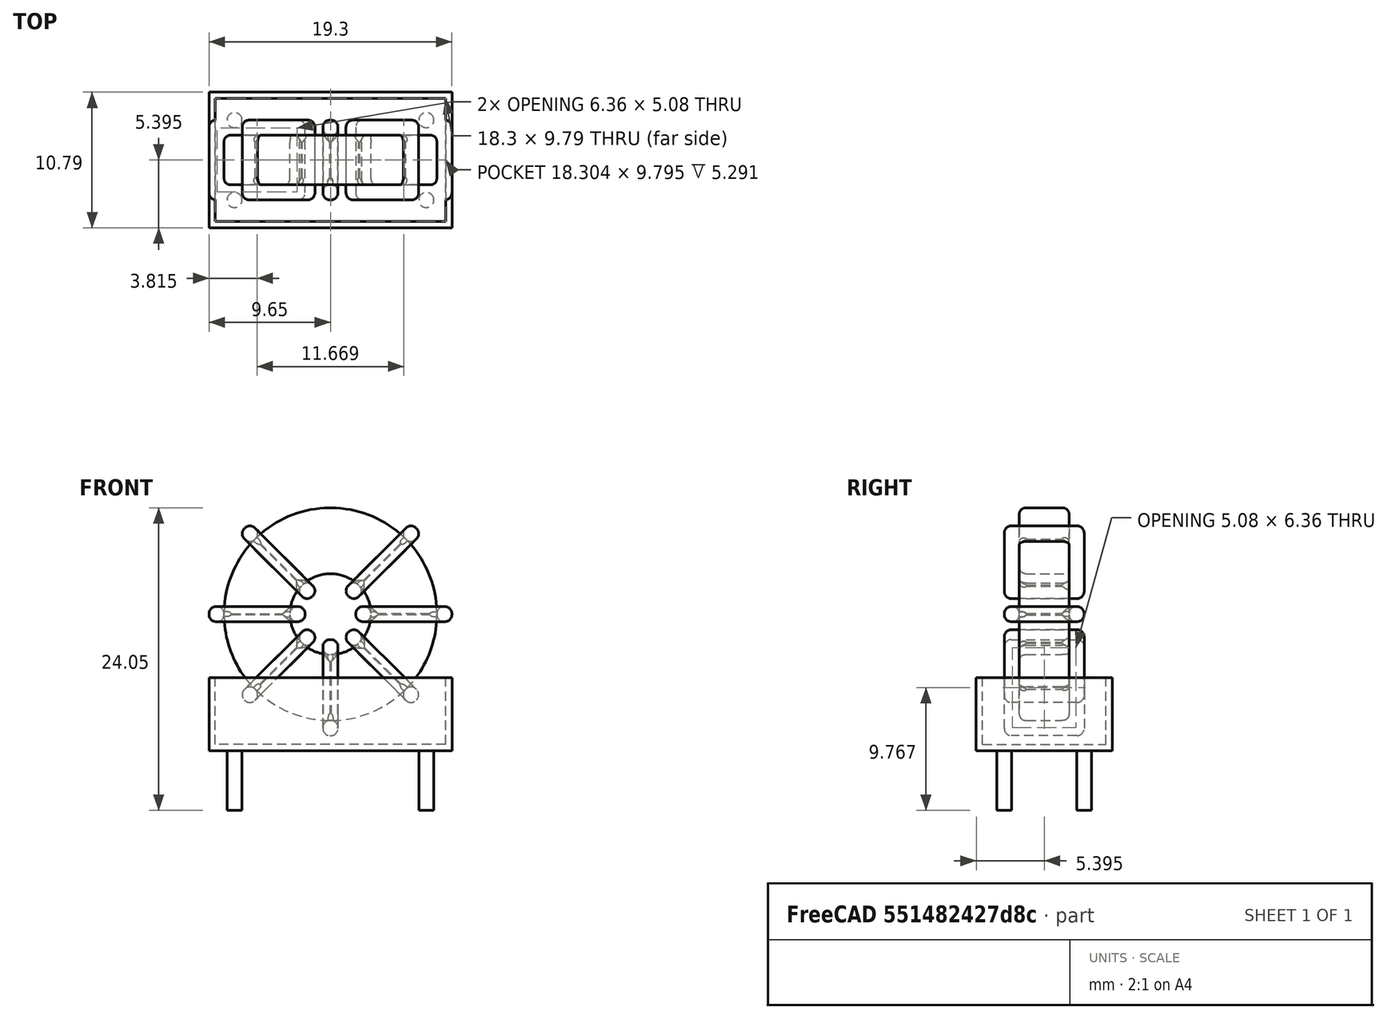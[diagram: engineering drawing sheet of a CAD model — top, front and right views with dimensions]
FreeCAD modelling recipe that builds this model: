
FCSTD DOCUMENT  (FreeCAD 0.16R6712 (Git))
Label: L_CommonMode_Toroid_Vertical_L19.3mm_W10.8mm_Px6.35mm_Py15.24mm_Bourns_8100
License: All rights reserved
LicenseURL: http://en.wikipedia.org/wiki/All_rights_reserved
objects: Sketcher::SketchObject×8, PartDesign::Pad×8, PartDesign::Fillet×5, Spreadsheet::Sheet×1, Part::MultiFuse×1
note: 30 computed .brp shape members not serialized (recipe doc carries the construction recipe); baked Part::Feature solids carry a one-line shape summary decoded from their .brp

FEATURE [Spreadsheet::Sheet] Spreadsheet  label="dimensions"
  cells = A1=Wx; B1(Wx)=19.304; C1(WW)=6.434666666666666; D1(iWx)=19.304; A2=Wy; B2(Wy)=6.35; D2(iWy)=10.795; A3=RM; B3(RMx)=6.35; C3(RMy)=15.24; A4=d_wire; B4(d_wire)=1.2; A5=H; B5(H)=31; A6=offsetx; B6(offsetx)=2.032
FEATURE [Sketcher::SketchObject] Sketch
  Placement = pos=(7.62,-3.175,0) rot=(1,0,0;1.5708rad)
  expr: Placement.Base.x = Spreadsheet.RMy / 2
  expr: Constraints[4] = Spreadsheet.WW / 2
  expr: Placement.Base.y = -Spreadsheet.RMx / 2
  expr: Constraints[0] = Spreadsheet.Wx / 2 - Spreadsheet.d_wire
  expr: Constraints[2] = Spreadsheet.Wx / 2 + Spreadsheet.d_wire + 0.5
  sketch-geometry (2):
    g0: Circle CenterX=0 CenterY=11.352 CenterZ=0 NormalX=0 NormalY=0 NormalZ=1 Radius=8.452
    g1: Circle CenterX=0 CenterY=11.352 CenterZ=0 NormalX=0 NormalY=0 NormalZ=1 Radius=3.21733
  constraints (5):
    c: Radius(g0) = 8.452
    c: DistanceX(g-1,g0) = 0
    c: DistanceY(g-1,g0) = 11.352
    c: Coincident(g1,g0)
    c: Radius(g1) = 3.21733
FEATURE [PartDesign::Pad] Pad
  Length = 3.95
  Length2 = 100
  Midplane = true
  Placement = pos=(7.62,-3.175,0) rot=(1,0,0;1.5708rad)
  Sketch = -> Sketch
  Type = 0
  expr: Length = Spreadsheet.Wy - 2 * Spreadsheet.d_wire
FEATURE [Sketcher::SketchObject] Sketch001
  Placement = pos=(0,0,0.75) rot=(0,0,1;0rad)
  expr: Constraints[4] = Spreadsheet.RMy
  expr: Constraints[2] = -Spreadsheet.RMx
  expr: Constraints[1] = Spreadsheet.d_wire / 2
  sketch-geometry (4):
    g0: Circle CenterX=0 CenterY=0 CenterZ=0 NormalX=0 NormalY=0 NormalZ=1 Radius=0.6
    g1: Circle CenterX=15.24 CenterY=-6.35 CenterZ=0 NormalX=0 NormalY=0 NormalZ=1 Radius=0.6
    g2: Circle CenterX=0 CenterY=-6.35 CenterZ=0 NormalX=0 NormalY=0 NormalZ=1 Radius=0.6
    g3: Circle CenterX=15.24 CenterY=0 CenterZ=0 NormalX=0 NormalY=0 NormalZ=1 Radius=0.6
  constraints (11):
    c: Equal(g0,g1)
    c: Radius(g0) = 0.6
    c: DistanceY(g-1,g1) = -6.35
    c: Coincident(g0,g-1)
    c: DistanceX(g-1,g1) = 15.24
    c: PointOnObject(g2,g-2)
    c: DistanceY(g-1,g3) = 0
    c: DistanceY(g2,g1) = 0
    c: DistanceX(g3,g1) = 0
    c: Equal(g3,g2)
    c: Equal(g2,g1)
FEATURE [PartDesign::Pad] Pad001
  Length = 5
  Length2 = 0
  Placement = pos=(0,0,0.75) rot=(0,0,1;0rad)
  Reversed = true
  Sketch = -> Sketch001
  Type = 0
FEATURE [PartDesign::Fillet] Fillet
  Base = -> Pad [Edge6,Edge3,Edge2]
  Placement = pos=(7.62,-3.175,0) rot=(1,0,0;1.5708rad)
  Radius = 0.5
FEATURE [Sketcher::SketchObject] Sketch003
  Placement = pos=(7.62,0,11.352) rot=(1,0,0;3.14159rad)
  expr: Placement.Base.x = Spreadsheet.RMy / 2
  expr: Constraints[18] = Spreadsheet.d_wire
  expr: Constraints[16] = Spreadsheet.d_wire
  expr: Constraints[19] = Spreadsheet.d_wire
  expr: Constraints[17] = Spreadsheet.d_wire
  expr: Placement.Base.y = -1 * (Spreadsheet.RMx - Spreadsheet.Wy) / 2
  expr: Constraints[21] = (Spreadsheet.Wx - Spreadsheet.WW) / 2 - Spreadsheet.d_wire
  expr: Constraints[22] = Spreadsheet.Wx / 2 - Spreadsheet.d_wire
  expr: Constraints[43] = Spreadsheet.d_wire
  expr: Constraints[48] = Spreadsheet.Wx - Spreadsheet.d_wire * 2
  expr: Constraints[49] = Spreadsheet.Wy
  expr: Placement.Base.z = Spreadsheet.Wx / 2 + Spreadsheet.d_wire + 0.5
  sketch-geometry (16):
    g0: LineSegment StartX=-2.01733 StartY=0 StartZ=0 EndX=-9.652 EndY=0 EndZ=0
    g1: LineSegment StartX=-9.652 StartY=0 StartZ=0 EndX=-9.652 EndY=6.35 EndZ=0
    g2: LineSegment StartX=-9.652 StartY=6.35 StartZ=0 EndX=-2.01733 EndY=6.35 EndZ=0
    g3: LineSegment StartX=-2.01733 StartY=6.35 StartZ=0 EndX=-2.01733 EndY=0 EndZ=0
    g4: LineSegment StartX=-8.452 StartY=5.15 StartZ=0 EndX=-3.21733 EndY=5.15 EndZ=0
    g5: LineSegment StartX=-3.21733 StartY=5.15 StartZ=0 EndX=-3.21733 EndY=1.2 EndZ=0
    g6: LineSegment StartX=-3.21733 StartY=1.2 StartZ=0 EndX=-8.452 EndY=1.2 EndZ=0
    g7: LineSegment StartX=-8.452 StartY=1.2 StartZ=0 EndX=-8.452 EndY=5.15 EndZ=0
    g8: LineSegment StartX=2.01733 StartY=6.35 StartZ=0 EndX=9.652 EndY=6.35 EndZ=0
    g9: LineSegment StartX=9.652 StartY=6.35 StartZ=0 EndX=9.652 EndY=0 EndZ=0
    g10: LineSegment StartX=9.652 StartY=0 StartZ=0 EndX=2.01733 EndY=0 EndZ=0
    g11: LineSegment StartX=2.01733 StartY=0 StartZ=0 EndX=2.01733 EndY=6.35 EndZ=0
    g12: LineSegment StartX=3.21733 StartY=5.15 StartZ=0 EndX=8.452 EndY=5.15 EndZ=0
    g13: LineSegment StartX=8.452 StartY=5.15 StartZ=0 EndX=8.452 EndY=1.2 EndZ=0
    g14: LineSegment StartX=8.452 StartY=1.2 StartZ=0 EndX=3.21733 EndY=1.2 EndZ=0
    g15: LineSegment StartX=3.21733 StartY=1.2 StartZ=0 EndX=3.21733 EndY=5.15 EndZ=0
  constraints (50):
    c: Horizontal(g0)
    c: Coincident(g1,g0)
    c: Vertical(g1)
    c: Coincident(g2,g1)
    c: Horizontal(g2)
    c: Coincident(g3,g2)
    c: Coincident(g3,g0)
    c: Vertical(g3)
    c: Coincident(g4,g5)
    c: Coincident(g5,g6)
    c: Coincident(g6,g7)
    c: Coincident(g7,g4)
    c: Horizontal(g4)
    c: Horizontal(g6)
    c: Vertical(g5)
    c: Vertical(g7)
    c: DistanceX(g1,g4) = 1.2
    c: DistanceY(g4,g1) = 1.2
    c: DistanceX(g5,g0) = 1.2
    c: DistanceY(g0,g5) = 1.2
    c: DistanceY(g-1,g0) = 0
    c: DistanceX(g6,g6) = 5.23467
    c: DistanceX(g6,g-1) = 8.452
    c: Coincident(g8,g9)
    c: Coincident(g9,g10)
    c: Coincident(g10,g11)
    c: Coincident(g11,g8)
    c: Horizontal(g8)
    c: Horizontal(g10)
    c: Vertical(g9)
    c: Vertical(g11)
    c: Coincident(g12,g13)
    c: Coincident(g13,g14)
    c: Coincident(g14,g15)
    c: Coincident(g15,g12)
    c: Horizontal(g12)
    c: Horizontal(g14)
    c: Vertical(g13)
    c: Vertical(g15)
    c: DistanceY(g8,g2) = 0
    c: DistanceY(g10,g0) = 0
    c: DistanceY(g14,g5) = 0
    c: DistanceY(g12,g4) = 0
    c: DistanceX(g8,g12) = 1.2
    c: Equal(g8,g2)
    c: Equal(g12,g4)
    c: Equal(g9,g1)
    c: Equal(g13,g7)
    c: DistanceX(g4,g12) = 16.904
    c: DistanceY(g0,g1) = 6.35
FEATURE [PartDesign::Pad] Pad002
  Length = 1.2
  Length2 = 100
  Midplane = true
  Placement = pos=(7.62,0,11.352) rot=(1,0,0;3.14159rad)
  Sketch = -> Sketch003
  Type = 0
  expr: Length = Spreadsheet.d_wire
FEATURE [PartDesign::Fillet] Fillet001
  Base = -> Pad002 [Edge38,Edge41,Edge42,Edge43,Edge29,Edge32,Edge33,Edge34,Edge25,Edge35,Edge36,Edge13,Edge14,Edge15,Edge16,Edge17,Edge18,Edge19,Edge1,Edge2,Edge3,Edge4,Edge5,Edge6,Edge7,Edge37,Edge39,Edge40,Edge20,Edge23,Edge24,Edge21,Edge22,Edge8,Edge9,Edge10,Edge11,Edge12,Edge26,Edge27,+8 more]
  Placement = pos=(7.62,0,11.352) rot=(1,0,0;3.14159rad)
  Radius = 0.564
  expr: Radius = Spreadsheet.d_wire * 0.47
FEATURE [Sketcher::SketchObject] Sketch004
  Placement = pos=(7.62,0,11.352) rot=(0.92388,0,0.382683;3.14159rad)
  expr: Placement.Base.x = Spreadsheet.RMy / 2
  expr: Constraints[18] = Spreadsheet.d_wire
  expr: Constraints[16] = Spreadsheet.d_wire
  expr: Constraints[19] = Spreadsheet.d_wire
  expr: Constraints[17] = Spreadsheet.d_wire
  expr: Placement.Base.y = -1 * (Spreadsheet.RMx - Spreadsheet.Wy) / 2
  expr: Constraints[21] = (Spreadsheet.Wx - Spreadsheet.WW) / 2 - Spreadsheet.d_wire
  expr: Constraints[22] = Spreadsheet.Wx / 2 - Spreadsheet.d_wire
  expr: Constraints[43] = Spreadsheet.d_wire
  expr: Constraints[48] = Spreadsheet.Wx - 2 * Spreadsheet.d_wire
  expr: Constraints[49] = Spreadsheet.Wy
  expr: Placement.Base.z = Spreadsheet.Wx / 2 + Spreadsheet.d_wire + 0.5
  sketch-geometry (16):
    g0: LineSegment StartX=-2.01733 StartY=0 StartZ=0 EndX=-9.652 EndY=0 EndZ=0
    g1: LineSegment StartX=-9.652 StartY=0 StartZ=0 EndX=-9.652 EndY=6.35 EndZ=0
    g2: LineSegment StartX=-9.652 StartY=6.35 StartZ=0 EndX=-2.01733 EndY=6.35 EndZ=0
    g3: LineSegment StartX=-2.01733 StartY=6.35 StartZ=0 EndX=-2.01733 EndY=0 EndZ=0
    g4: LineSegment StartX=-8.452 StartY=5.15 StartZ=0 EndX=-3.21733 EndY=5.15 EndZ=0
    g5: LineSegment StartX=-3.21733 StartY=5.15 StartZ=0 EndX=-3.21733 EndY=1.2 EndZ=0
    g6: LineSegment StartX=-3.21733 StartY=1.2 StartZ=0 EndX=-8.452 EndY=1.2 EndZ=0
    g7: LineSegment StartX=-8.452 StartY=1.2 StartZ=0 EndX=-8.452 EndY=5.15 EndZ=0
    g8: LineSegment StartX=2.01733 StartY=6.35 StartZ=0 EndX=9.652 EndY=6.35 EndZ=0
    g9: LineSegment StartX=9.652 StartY=6.35 StartZ=0 EndX=9.652 EndY=0 EndZ=0
    g10: LineSegment StartX=9.652 StartY=0 StartZ=0 EndX=2.01733 EndY=0 EndZ=0
    g11: LineSegment StartX=2.01733 StartY=0 StartZ=0 EndX=2.01733 EndY=6.35 EndZ=0
    g12: LineSegment StartX=3.21733 StartY=5.15 StartZ=0 EndX=8.452 EndY=5.15 EndZ=0
    g13: LineSegment StartX=8.452 StartY=5.15 StartZ=0 EndX=8.452 EndY=1.2 EndZ=0
    g14: LineSegment StartX=8.452 StartY=1.2 StartZ=0 EndX=3.21733 EndY=1.2 EndZ=0
    g15: LineSegment StartX=3.21733 StartY=1.2 StartZ=0 EndX=3.21733 EndY=5.15 EndZ=0
  constraints (50):
    c: Horizontal(g0)
    c: Coincident(g1,g0)
    c: Vertical(g1)
    c: Coincident(g2,g1)
    c: Horizontal(g2)
    c: Coincident(g3,g2)
    c: Coincident(g3,g0)
    c: Vertical(g3)
    c: Coincident(g4,g5)
    c: Coincident(g5,g6)
    c: Coincident(g6,g7)
    c: Coincident(g7,g4)
    c: Horizontal(g4)
    c: Horizontal(g6)
    c: Vertical(g5)
    c: Vertical(g7)
    c: DistanceX(g1,g4) = 1.2
    c: DistanceY(g4,g1) = 1.2
    c: DistanceX(g5,g0) = 1.2
    c: DistanceY(g0,g5) = 1.2
    c: DistanceY(g-1,g0) = 0
    c: DistanceX(g6,g6) = 5.23467
    c: DistanceX(g6,g-1) = 8.452
    c: Coincident(g8,g9)
    c: Coincident(g9,g10)
    c: Coincident(g10,g11)
    c: Coincident(g11,g8)
    c: Horizontal(g8)
    c: Horizontal(g10)
    c: Vertical(g9)
    c: Vertical(g11)
    c: Coincident(g12,g13)
    c: Coincident(g13,g14)
    c: Coincident(g14,g15)
    c: Coincident(g15,g12)
    c: Horizontal(g12)
    c: Horizontal(g14)
    c: Vertical(g13)
    c: Vertical(g15)
    c: DistanceY(g8,g2) = 0
    c: DistanceY(g10,g0) = 0
    c: DistanceY(g14,g5) = 0
    c: DistanceY(g12,g4) = 0
    c: DistanceX(g8,g12) = 1.2
    c: Equal(g8,g2)
    c: Equal(g12,g4)
    c: Equal(g9,g1)
    c: Equal(g13,g7)
    c: DistanceX(g4,g12) = 16.904
    c: DistanceY(g0,g1) = 6.35
FEATURE [PartDesign::Pad] Pad003
  Length = 1.2
  Length2 = 100
  Midplane = true
  Placement = pos=(7.62,0,11.352) rot=(0.92388,0,0.382683;3.14159rad)
  Sketch = -> Sketch004
  Type = 0
  expr: Length = Spreadsheet.d_wire
FEATURE [PartDesign::Fillet] Fillet002
  Base = -> Pad003 [Edge38,Edge41,Edge42,Edge43,Edge29,Edge32,Edge33,Edge34,Edge25,Edge35,Edge36,Edge13,Edge14,Edge15,Edge16,Edge17,Edge18,Edge19,Edge1,Edge2,Edge3,Edge4,Edge5,Edge6,Edge7,Edge37,Edge39,Edge40,Edge20,Edge23,Edge24,Edge21,Edge22,Edge8,Edge9,Edge10,Edge11,Edge12,Edge26,Edge27,+8 more]
  Placement = pos=(7.62,0,11.352) rot=(0.92388,0,0.382683;3.14159rad)
  Radius = 0.564
  expr: Radius = Spreadsheet.d_wire * 0.47
FEATURE [Sketcher::SketchObject] Sketch005
  Placement = pos=(7.62,0,11.352) rot=(0.92388,0,-0.382683;3.14159rad)
  expr: Placement.Base.x = Spreadsheet.RMy / 2
  expr: Constraints[18] = Spreadsheet.d_wire
  expr: Constraints[16] = Spreadsheet.d_wire
  expr: Constraints[19] = Spreadsheet.d_wire
  expr: Constraints[17] = Spreadsheet.d_wire
  expr: Placement.Base.y = -1 * (Spreadsheet.RMx - Spreadsheet.Wy) / 2
  expr: Constraints[21] = (Spreadsheet.Wx - Spreadsheet.WW) / 2 - Spreadsheet.d_wire
  expr: Constraints[22] = Spreadsheet.Wx / 2 - Spreadsheet.d_wire
  expr: Constraints[43] = Spreadsheet.d_wire
  expr: Constraints[48] = Spreadsheet.Wx - 2 * Spreadsheet.d_wire
  expr: Constraints[49] = Spreadsheet.Wy
  expr: Placement.Base.z = Spreadsheet.Wx / 2 + Spreadsheet.d_wire + 0.5
  sketch-geometry (16):
    g0: LineSegment StartX=-2.01733 StartY=0 StartZ=0 EndX=-9.652 EndY=0 EndZ=0
    g1: LineSegment StartX=-9.652 StartY=0 StartZ=0 EndX=-9.652 EndY=6.35 EndZ=0
    g2: LineSegment StartX=-9.652 StartY=6.35 StartZ=0 EndX=-2.01733 EndY=6.35 EndZ=0
    g3: LineSegment StartX=-2.01733 StartY=6.35 StartZ=0 EndX=-2.01733 EndY=0 EndZ=0
    g4: LineSegment StartX=-8.452 StartY=5.15 StartZ=0 EndX=-3.21733 EndY=5.15 EndZ=0
    g5: LineSegment StartX=-3.21733 StartY=5.15 StartZ=0 EndX=-3.21733 EndY=1.2 EndZ=0
    g6: LineSegment StartX=-3.21733 StartY=1.2 StartZ=0 EndX=-8.452 EndY=1.2 EndZ=0
    g7: LineSegment StartX=-8.452 StartY=1.2 StartZ=0 EndX=-8.452 EndY=5.15 EndZ=0
    g8: LineSegment StartX=2.01733 StartY=6.35 StartZ=0 EndX=9.652 EndY=6.35 EndZ=0
    g9: LineSegment StartX=9.652 StartY=6.35 StartZ=0 EndX=9.652 EndY=0 EndZ=0
    g10: LineSegment StartX=9.652 StartY=0 StartZ=0 EndX=2.01733 EndY=0 EndZ=0
    g11: LineSegment StartX=2.01733 StartY=0 StartZ=0 EndX=2.01733 EndY=6.35 EndZ=0
    g12: LineSegment StartX=3.21733 StartY=5.15 StartZ=0 EndX=8.452 EndY=5.15 EndZ=0
    g13: LineSegment StartX=8.452 StartY=5.15 StartZ=0 EndX=8.452 EndY=1.2 EndZ=0
    g14: LineSegment StartX=8.452 StartY=1.2 StartZ=0 EndX=3.21733 EndY=1.2 EndZ=0
    g15: LineSegment StartX=3.21733 StartY=1.2 StartZ=0 EndX=3.21733 EndY=5.15 EndZ=0
  constraints (50):
    c: Horizontal(g0)
    c: Coincident(g1,g0)
    c: Vertical(g1)
    c: Coincident(g2,g1)
    c: Horizontal(g2)
    c: Coincident(g3,g2)
    c: Coincident(g3,g0)
    c: Vertical(g3)
    c: Coincident(g4,g5)
    c: Coincident(g5,g6)
    c: Coincident(g6,g7)
    c: Coincident(g7,g4)
    c: Horizontal(g4)
    c: Horizontal(g6)
    c: Vertical(g5)
    c: Vertical(g7)
    c: DistanceX(g1,g4) = 1.2
    c: DistanceY(g4,g1) = 1.2
    c: DistanceX(g5,g0) = 1.2
    c: DistanceY(g0,g5) = 1.2
    c: DistanceY(g-1,g0) = 0
    c: DistanceX(g6,g6) = 5.23467
    c: DistanceX(g6,g-1) = 8.452
    c: Coincident(g8,g9)
    c: Coincident(g9,g10)
    c: Coincident(g10,g11)
    c: Coincident(g11,g8)
    c: Horizontal(g8)
    c: Horizontal(g10)
    c: Vertical(g9)
    c: Vertical(g11)
    c: Coincident(g12,g13)
    c: Coincident(g13,g14)
    c: Coincident(g14,g15)
    c: Coincident(g15,g12)
    c: Horizontal(g12)
    c: Horizontal(g14)
    c: Vertical(g13)
    c: Vertical(g15)
    c: DistanceY(g8,g2) = 0
    c: DistanceY(g10,g0) = 0
    c: DistanceY(g14,g5) = 0
    c: DistanceY(g12,g4) = 0
    c: DistanceX(g8,g12) = 1.2
    c: Equal(g8,g2)
    c: Equal(g12,g4)
    c: Equal(g9,g1)
    c: Equal(g13,g7)
    c: DistanceX(g4,g12) = 16.904
    c: DistanceY(g0,g1) = 6.35
FEATURE [PartDesign::Pad] Pad004
  Length = 1.2
  Length2 = 100
  Midplane = true
  Placement = pos=(7.62,0,11.352) rot=(0.92388,0,-0.382683;3.14159rad)
  Sketch = -> Sketch005
  Type = 0
  expr: Length = Spreadsheet.d_wire
FEATURE [PartDesign::Fillet] Fillet003
  Base = -> Pad004 [Edge38,Edge41,Edge42,Edge43,Edge29,Edge32,Edge33,Edge34,Edge25,Edge35,Edge36,Edge13,Edge14,Edge15,Edge16,Edge17,Edge18,Edge19,Edge1,Edge2,Edge3,Edge4,Edge5,Edge6,Edge7,Edge37,Edge39,Edge40,Edge20,Edge23,Edge24,Edge21,Edge22,Edge8,Edge9,Edge10,Edge11,Edge12,Edge26,Edge27,+8 more]
  Placement = pos=(7.62,0,11.352) rot=(0.92388,0,-0.382683;3.14159rad)
  Radius = 0.564
  expr: Radius = Spreadsheet.d_wire * 0.47
FEATURE [Sketcher::SketchObject] Sketch006
  Placement = pos=(7.62,0,11.352) rot=(0.707107,0,0.707107;3.14159rad)
  expr: Placement.Base.x = Spreadsheet.RMy / 2
  expr: Constraints[18] = Spreadsheet.d_wire
  expr: Constraints[16] = Spreadsheet.d_wire
  expr: Constraints[19] = Spreadsheet.d_wire
  expr: Constraints[17] = Spreadsheet.d_wire
  expr: Placement.Base.y = -1 * (Spreadsheet.RMx - Spreadsheet.Wy) / 2
  expr: Constraints[21] = (Spreadsheet.Wx - Spreadsheet.WW) / 2 - Spreadsheet.d_wire
  expr: Constraints[22] = Spreadsheet.Wx / 2 - Spreadsheet.d_wire
  expr: Constraints[43] = Spreadsheet.d_wire
  expr: Constraints[48] = Spreadsheet.Wx - Spreadsheet.d_wire * 2
  expr: Constraints[49] = Spreadsheet.Wy
  expr: Placement.Base.z = Spreadsheet.Wx / 2 + Spreadsheet.d_wire + 0.5
  sketch-geometry (16):
    g0: LineSegment StartX=-2.01733 StartY=0 StartZ=0 EndX=-9.652 EndY=0 EndZ=0
    g1: LineSegment StartX=-9.652 StartY=0 StartZ=0 EndX=-9.652 EndY=6.35 EndZ=0
    g2: LineSegment StartX=-9.652 StartY=6.35 StartZ=0 EndX=-2.01733 EndY=6.35 EndZ=0
    g3: LineSegment StartX=-2.01733 StartY=6.35 StartZ=0 EndX=-2.01733 EndY=0 EndZ=0
    g4: LineSegment StartX=-8.452 StartY=5.15 StartZ=0 EndX=-3.21733 EndY=5.15 EndZ=0
    g5: LineSegment StartX=-3.21733 StartY=5.15 StartZ=0 EndX=-3.21733 EndY=1.2 EndZ=0
    g6: LineSegment StartX=-3.21733 StartY=1.2 StartZ=0 EndX=-8.452 EndY=1.2 EndZ=0
    g7: LineSegment StartX=-8.452 StartY=1.2 StartZ=0 EndX=-8.452 EndY=5.15 EndZ=0
    g8: LineSegment StartX=2.01733 StartY=6.35 StartZ=0 EndX=9.652 EndY=6.35 EndZ=0
    g9: LineSegment StartX=9.652 StartY=6.35 StartZ=0 EndX=9.652 EndY=0 EndZ=0
    g10: LineSegment StartX=9.652 StartY=0 StartZ=0 EndX=2.01733 EndY=0 EndZ=0
    g11: LineSegment StartX=2.01733 StartY=0 StartZ=0 EndX=2.01733 EndY=6.35 EndZ=0
    g12: LineSegment StartX=3.21733 StartY=5.15 StartZ=0 EndX=8.452 EndY=5.15 EndZ=0
    g13: LineSegment StartX=8.452 StartY=5.15 StartZ=0 EndX=8.452 EndY=1.2 EndZ=0
    g14: LineSegment StartX=8.452 StartY=1.2 StartZ=0 EndX=3.21733 EndY=1.2 EndZ=0
    g15: LineSegment StartX=3.21733 StartY=1.2 StartZ=0 EndX=3.21733 EndY=5.15 EndZ=0
  constraints (50):
    c: Horizontal(g0)
    c: Coincident(g1,g0)
    c: Vertical(g1)
    c: Coincident(g2,g1)
    c: Horizontal(g2)
    c: Coincident(g3,g2)
    c: Coincident(g3,g0)
    c: Vertical(g3)
    c: Coincident(g4,g5)
    c: Coincident(g5,g6)
    c: Coincident(g6,g7)
    c: Coincident(g7,g4)
    c: Horizontal(g4)
    c: Horizontal(g6)
    c: Vertical(g5)
    c: Vertical(g7)
    c: DistanceX(g1,g4) = 1.2
    c: DistanceY(g4,g1) = 1.2
    c: DistanceX(g5,g0) = 1.2
    c: DistanceY(g0,g5) = 1.2
    c: DistanceY(g-1,g0) = 0
    c: DistanceX(g6,g6) = 5.23467
    c: DistanceX(g6,g-1) = 8.452
    c: Coincident(g8,g9)
    c: Coincident(g9,g10)
    c: Coincident(g10,g11)
    c: Coincident(g11,g8)
    c: Horizontal(g8)
    c: Horizontal(g10)
    c: Vertical(g9)
    c: Vertical(g11)
    c: Coincident(g12,g13)
    c: Coincident(g13,g14)
    c: Coincident(g14,g15)
    c: Coincident(g15,g12)
    c: Horizontal(g12)
    c: Horizontal(g14)
    c: Vertical(g13)
    c: Vertical(g15)
    c: DistanceY(g8,g2) = 0
    c: DistanceY(g10,g0) = 0
    c: DistanceY(g14,g5) = 0
    c: DistanceY(g12,g4) = 0
    c: DistanceX(g8,g12) = 1.2
    c: Equal(g8,g2)
    c: Equal(g12,g4)
    c: Equal(g9,g1)
    c: Equal(g13,g7)
    c: DistanceX(g4,g12) = 16.904
    c: DistanceY(g0,g1) = 6.35
FEATURE [PartDesign::Pad] Pad005
  Length = 1.2
  Length2 = 100
  Midplane = true
  Placement = pos=(7.62,0,11.352) rot=(0.707107,0,0.707107;3.14159rad)
  Sketch = -> Sketch006
  Type = 0
  expr: Length = Spreadsheet.d_wire
FEATURE [PartDesign::Fillet] Fillet004
  Base = -> Pad005 [Edge38,Edge41,Edge42,Edge43,Edge29,Edge32,Edge33,Edge34,Edge25,Edge35,Edge36,Edge13,Edge14,Edge15,Edge16,Edge17,Edge18,Edge19,Edge1,Edge2,Edge3,Edge4,Edge5,Edge6,Edge7,Edge37,Edge39,Edge40,Edge20,Edge23,Edge24,Edge21,Edge22,Edge8,Edge9,Edge10,Edge11,Edge12,Edge26,Edge27,+8 more]
  Placement = pos=(7.62,0,11.352) rot=(0.707107,0,0.707107;3.14159rad)
  Radius = 0.564
  expr: Radius = Spreadsheet.d_wire * 0.47
FEATURE [Sketcher::SketchObject] Sketch007
  Placement = pos=(7.62,0,0.5) rot=(0,0,1;0rad)
  expr: Placement.Base.x = Spreadsheet.RMy / 2
  expr: Placement.Base.z = 0.5
  expr: Constraints[11] = Spreadsheet.iWx / 2
  expr: Constraints[10] = (Spreadsheet.iWy - Spreadsheet.RMx) / 2
  expr: Constraints[9] = Spreadsheet.iWy
  expr: Constraints[8] = Spreadsheet.iWx
  sketch-geometry (4):
    g0: LineSegment StartX=-9.652 StartY=2.2225 StartZ=0 EndX=9.652 EndY=2.2225 EndZ=0
    g1: LineSegment StartX=9.652 StartY=2.2225 StartZ=0 EndX=9.652 EndY=-8.5725 EndZ=0
    g2: LineSegment StartX=9.652 StartY=-8.5725 StartZ=0 EndX=-9.652 EndY=-8.5725 EndZ=0
    g3: LineSegment StartX=-9.652 StartY=-8.5725 StartZ=0 EndX=-9.652 EndY=2.2225 EndZ=0
  constraints (12):
    c: Coincident(g0,g1)
    c: Coincident(g1,g2)
    c: Coincident(g2,g3)
    c: Coincident(g3,g0)
    c: Horizontal(g0)
    c: Horizontal(g2)
    c: Vertical(g1)
    c: Vertical(g3)
    c: DistanceX(g0,g0) = 19.304
    c: DistanceY(g3,g3) = 10.795
    c: DistanceY(g-1,g0) = 2.2225
    c: DistanceX(g0,g-1) = 9.652
FEATURE [PartDesign::Pad] Pad006
  Length = 0.5
  Length2 = 100
  Placement = pos=(7.62,0,0.5) rot=(0,0,1;0rad)
  Sketch = -> Sketch007
  Type = 0
FEATURE [Sketcher::SketchObject] Sketch008
  Placement = pos=(7.62,0,0.5) rot=(0,0,1;0rad)
  expr: Placement.Base.x = Spreadsheet.RMy / 2
  expr: Constraints[8] = Spreadsheet.iWx
  expr: Constraints[9] = Spreadsheet.iWy
  expr: Constraints[10] = (Spreadsheet.iWy - Spreadsheet.RMx) / 2
  expr: Placement.Base.z = 0.5
  expr: Constraints[21] = 0.5
  expr: Constraints[11] = Spreadsheet.iWx / 2
  sketch-geometry (8):
    g0: LineSegment StartX=-9.652 StartY=2.2225 StartZ=0 EndX=9.652 EndY=2.2225 EndZ=0
    g1: LineSegment StartX=9.652 StartY=2.2225 StartZ=0 EndX=9.652 EndY=-8.5725 EndZ=0
    g2: LineSegment StartX=9.652 StartY=-8.5725 StartZ=0 EndX=-9.652 EndY=-8.5725 EndZ=0
    g3: LineSegment StartX=-9.652 StartY=-8.5725 StartZ=0 EndX=-9.652 EndY=2.2225 EndZ=0
    g4: LineSegment StartX=-9.152 StartY=1.7225 StartZ=0 EndX=9.152 EndY=1.7225 EndZ=0
    g5: LineSegment StartX=9.152 StartY=1.7225 StartZ=0 EndX=9.152 EndY=-8.0725 EndZ=0
    g6: LineSegment StartX=9.152 StartY=-8.0725 StartZ=0 EndX=-9.152 EndY=-8.0725 EndZ=0
    g7: LineSegment StartX=-9.152 StartY=-8.0725 StartZ=0 EndX=-9.152 EndY=1.7225 EndZ=0
  constraints (24):
    c: Coincident(g0,g1)
    c: Coincident(g1,g2)
    c: Coincident(g2,g3)
    c: Coincident(g3,g0)
    c: Horizontal(g0)
    c: Horizontal(g2)
    c: Vertical(g1)
    c: Vertical(g3)
    c: DistanceX(g0,g0) = 19.304
    c: DistanceY(g3,g3) = 10.795
    c: DistanceY(g-1,g0) = 2.2225
    c: DistanceX(g0,g-1) = 9.652
    c: Coincident(g4,g5)
    c: Coincident(g5,g6)
    c: Coincident(g6,g7)
    c: Coincident(g7,g4)
    c: Horizontal(g4)
    c: Horizontal(g6)
    c: Vertical(g5)
    c: Vertical(g7)
    c: DistanceX(g5,g1) = 0.5
    c: DistanceY(g1,g5) = 0.5
    c: DistanceX(g0,g4) = 0.5
    c: DistanceY(g4,g0) = 0.5
FEATURE [PartDesign::Pad] Pad007
  Length = 5.7912
  Length2 = 100
  Placement = pos=(7.62,0,0.5) rot=(0,0,1;0rad)
  Sketch = -> Sketch008
  Type = 0
  expr: Length = Spreadsheet.Wx * 0.3
FEATURE [Part::MultiFuse] Pad001_mp_cp  label="L_CommonMode_Toroid_Vertical_L19.3mm_W10.8mm_Px6.35mm_Py15.24mm_Bourns_8100"
  Shapes = -> [Pad001,Fillet,Fillet001,Fillet002,Fillet003,Fillet004,Pad006,Pad007]
